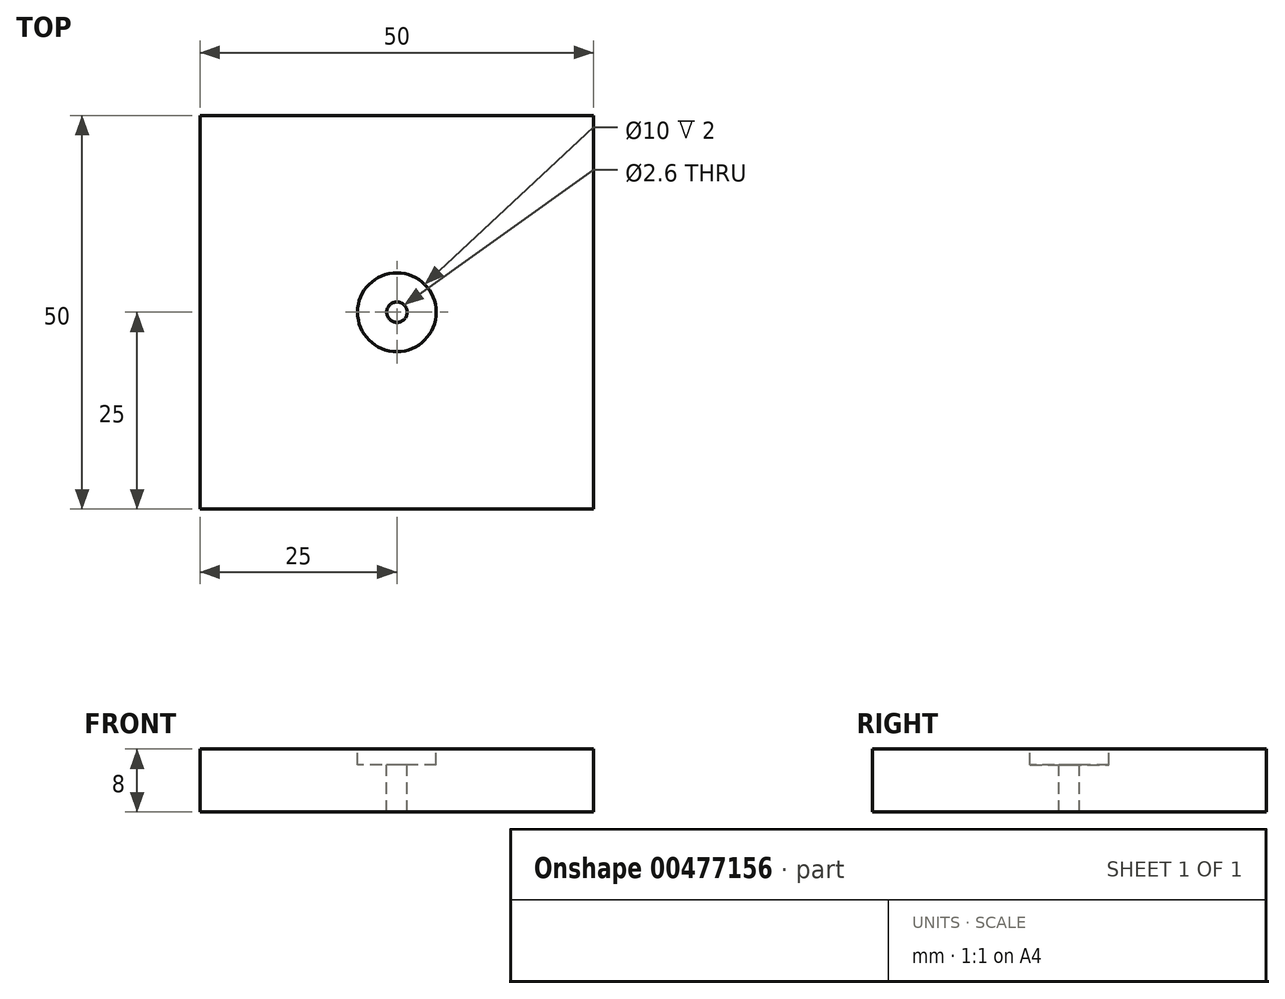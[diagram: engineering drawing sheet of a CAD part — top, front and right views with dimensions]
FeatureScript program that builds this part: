
annotation { "Feature Type Name" : "Feature", "Feature Type Description" : "" }
export const myFeature = defineFeature(function(context is Context, id is Id, definition is map)
    precondition{}
    {
        {
            var Q0;
            Q0=qCreatedBy(makeId("Top.planeOp"),FACE);
            var sketch = newSketch(context, id + "F0", { "sketchPlane" : qUnion([Q0])});
            skLineSegment(sketch, "E0.bottom", {"start": v(-25, 25) * mm, "end": v(25, 25) * mm});
            skLineSegment(sketch, "E0.top", {"start": v(-25, -25) * mm, "end": v(25, -25) * mm});
            skLineSegment(sketch, "E0.left", {"start": v(-25, 25) * mm, "end": v(-25, -25) * mm});
            skLineSegment(sketch, "E0.right", {"start": v(25, 25) * mm, "end": v(25, -25) * mm});
            skSolve(sketch);
        }
        {
            var Q0;
            Q0=qSketchRegion(id+"F0",true);
            extrude(context, id + "F1", {"entities" : qUnion([Q0]), "oppositeDirection" : true, "depth" : 8 * mm});
        }
        {
            var Q0;
            Q0=makeQuery(id+"F1.opExtrude","CAP_FACE",FACE,{"disambiguationData":[OSD([sQuery(id+"F0.wireOp",EDGE,"E0.bottom"),sQuery(id+"F0.wireOp",EDGE,"E0.top"),sQuery(id+"F0.wireOp",EDGE,"E0.left"),sQuery(id+"F0.wireOp",EDGE,"E0.right")])],"isStart":true});
            var sketch = newSketch(context, id + "F2", { "sketchPlane" : qUnion([Q0])});
            skCircle(sketch, "E1", {"center": v(0, 0) * mm, "radius": 5 * mm});
            skSolve(sketch);
        }
        {
            var Q0;
            Q0=qSketchRegion(id+"F2",true);
            extrude(context, id + "F3", {"entities" : qUnion([Q0]), "operationType" : NewBodyOperationType.REMOVE, "oppositeDirection" : true, "depth" : 2 * mm});
        }
        {
            var Q0;
            Q0=makeQuery(id+"F3.boolean.opBoolean","COPY",FACE,{"derivedFrom":makeQuery(id+"F3.opExtrude","CAP_FACE",FACE,{"disambiguationData":[OSD([sQuery(id+"F2.wireOp",EDGE,"E1")])],"isStart":false})});
            var sketch = newSketch(context, id + "F4", { "sketchPlane" : qUnion([Q0])});
            skCircle(sketch, "E2", {"center": v(0, 0) * mm, "radius": 1.3 * mm});
            skSolve(sketch);
        }
        {
            var Q0;
            Q0=qSketchRegion(id+"F4",true);
            extrude(context, id + "F5", {"entities" : qUnion([Q0]), "operationType" : NewBodyOperationType.REMOVE, "endBound" : BoundingType.THROUGH_ALL, "oppositeDirection" : true, "depth" : 25 * mm, "offsetDistance" : 25 * mm});
        }
    });
